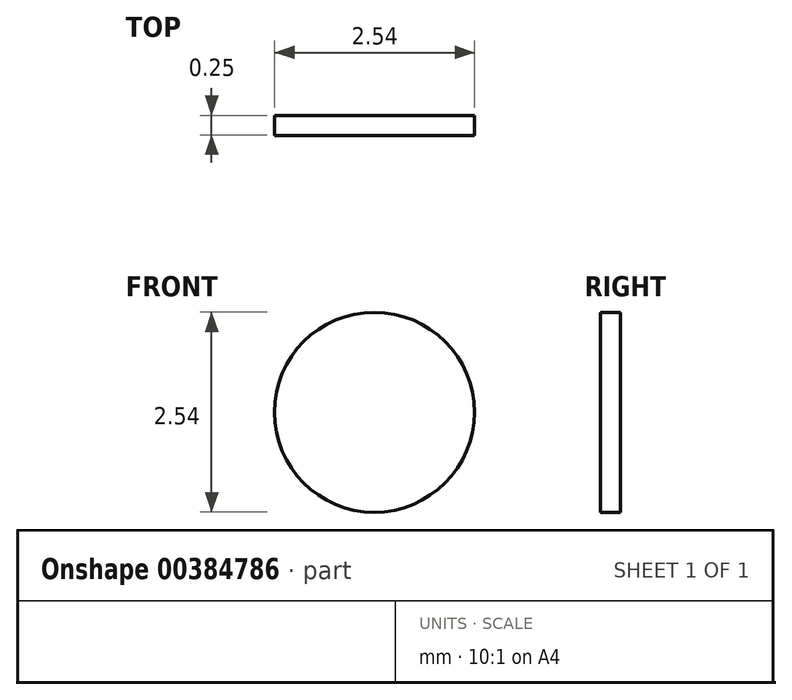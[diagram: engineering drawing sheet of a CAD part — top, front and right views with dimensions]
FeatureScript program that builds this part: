
annotation { "Feature Type Name" : "Feature", "Feature Type Description" : "" }
export const myFeature = defineFeature(function(context is Context, id is Id, definition is map)
    precondition{}
    {
        {
            var Q0;
            Q0=qCreatedBy(makeId("Front.planeOp"),FACE);
            var sketch = newSketch(context, id + "F0", { "sketchPlane" : qUnion([Q0])});
            skCircle(sketch, "E0", {"center": v(-48.6, 42.56) * mm, "radius": 1.27 * mm});
            skSolve(sketch);
        }
        {
            var Q0;
            Q0 = qSketchRegion(id + "F0", true);
            extrude(context, id + "F1", {"entities" : qUnion([Q0]), "depth" : 0.25 * mm});
        }
    });
